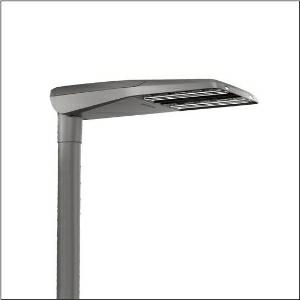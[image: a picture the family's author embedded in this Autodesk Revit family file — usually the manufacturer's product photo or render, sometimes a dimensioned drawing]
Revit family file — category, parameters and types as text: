
# Revit family: streetlight_sl_11_iq_midi___st1_2a_5xc3a41f08le_475e
name_source: partatom
category: Lighting Fixtures
units: mm (PartAtom-declared; Revit-internal decimal feet)

## family parameters
Cut with Voids When Loaded = No
Host = Face
Light Source = No
Part Type = Normal
Room Calculation Point = No
Round Connector Dimension = Use Diameter
Shared = No

## types (1)
- --- (1 x LED, 9590 lm, 60.4 W, 4000K)
    Apparent Load = 60 VA
    CIE Flux Codes = 32 70 96 100 100
    Color Rendering = 70
    Color Temperature = 4000K
    Default Elevation = 1800 mm
    Description = Streetlight SL 11 iQ midi, mast luminaire, primary light control with 3 zone facetted reflector, of plastic, silver coated, highly specular, primary optical cover: cover, of PMMA, transparent, light distribution: ST1.2a, light emission: direct distribution, primary light characteristic: asymmetric, installation type: post-top, side-entry, lamps: LED, High Power LED, rated values: 9.590lm | 60,4W | 158,8lm/W (begin service life); end service life: 9.590lm | 62,5W; at 50% lumin. flux: 4.795lm | 29,7W | 161,4lm/W, colour temperature: 4000K, colour rendering: CRI > 70, light colour: 740, light setting 1 begin service life: 100% | 9.590lm | 60,4W | 158,8lm/W | 4.000K, light setting 1 end service life: 62,5W, further light settings possible, control: Street-Remote, optimised constant luminous flux control (CLO 2.0), Desk-Remote (wireless, voltage-free reading and setting of iQ features in the workshop via application-optimized NFC function/RFID function), Light-Fading, Smart-Wire, Night-Set, Lumen-Switch, Temp-Guard, Auto-Match, with cable H07RN-F 3x 1.5mm², mains connection: 230..240V, AC, 50/60Hz, connection cable pre-assembled, cable length: 8,5m, luminaire housing, of diecast aluminium, powder-coated, SITECO metallic grey (DB 702S), please order mast flange separately, inclination adjustable without tools: 0°, 5°, 10°, 15° (post-top) | 0°, -5°, -10°, -15° (side-entry), sealing non-destructively replaceable, multi-level sealing system, length: 780mm, width: 376mm, height: 118mm, mast flange for spigot size: 42mm (side-entry): 5XC10008XM4, 60/48mm (side-entry/post-top): 5XC10108XM2, 76/60mm (side-entry/post-top): 5XC10108XM1, equipment: standard, protection rating (complete): IP66, insulation class (complete): insulation class II (safety insulation), certification: CE, ENEC, ENEC+, VDE, impact resistance: IK10, permissible operating ambient temperature for outdoor applications: -25..+50°C, standard-compliant lighting for roads and squares, Environmental Product Declaration (EPD) tested and certified by an independent institute, packaging unit: 1 piece

Light Distribution: ST1.2a
    Height = 118 mm
    Lamp = 1 x LED
    Lamp Light Flux = 9590 lm
    Lamp Power = 60.4 W
    Lamp count = 1
    Length = 780 mm
    Luminous efficacy = 159 lm/W
    Manufacturer = Siteco
    ModVariant = No
    Model = 5XC3A41F08LE
    Number of Poles = 1
    OnlyDefault = Yes
    Power Factor = 1
    Product Name = Streetlight SL 11 iQ midi | ST1.2a
    Product group = mast luminaire | pylon top
    ProductGroupID = 6100
    Protection Class = Protection class II
    Protection Degree = IP 66
    RLX_Detail_Level = 1
    RLX_Emergency_Light_Flux = 0 lm
    RLX_Emergency_Type = 0
    RLX_Emergency_Type_DB = No
    RlxData = <blob elided: 70793 chars, md5=37585e62>
    Socket = socket
    Standby Power = 0 W
    System Light Flux = 9590 lm
    System Power = 60 W
    Type Comments = factory setting: luminous flux: 100 % | dim-lin: 254 | 520 mA
    Type Image = l_1005960.jpg
    URL = http://relux.com
    VarID = @adj_194483
    Voltage = 0 V
    Weight = 0.00 kg
    Width = 376 mm

## geometry (parser evidence)
native form markers: Blend x4, Sweep x8
no freeform markers — native parametric forms only
